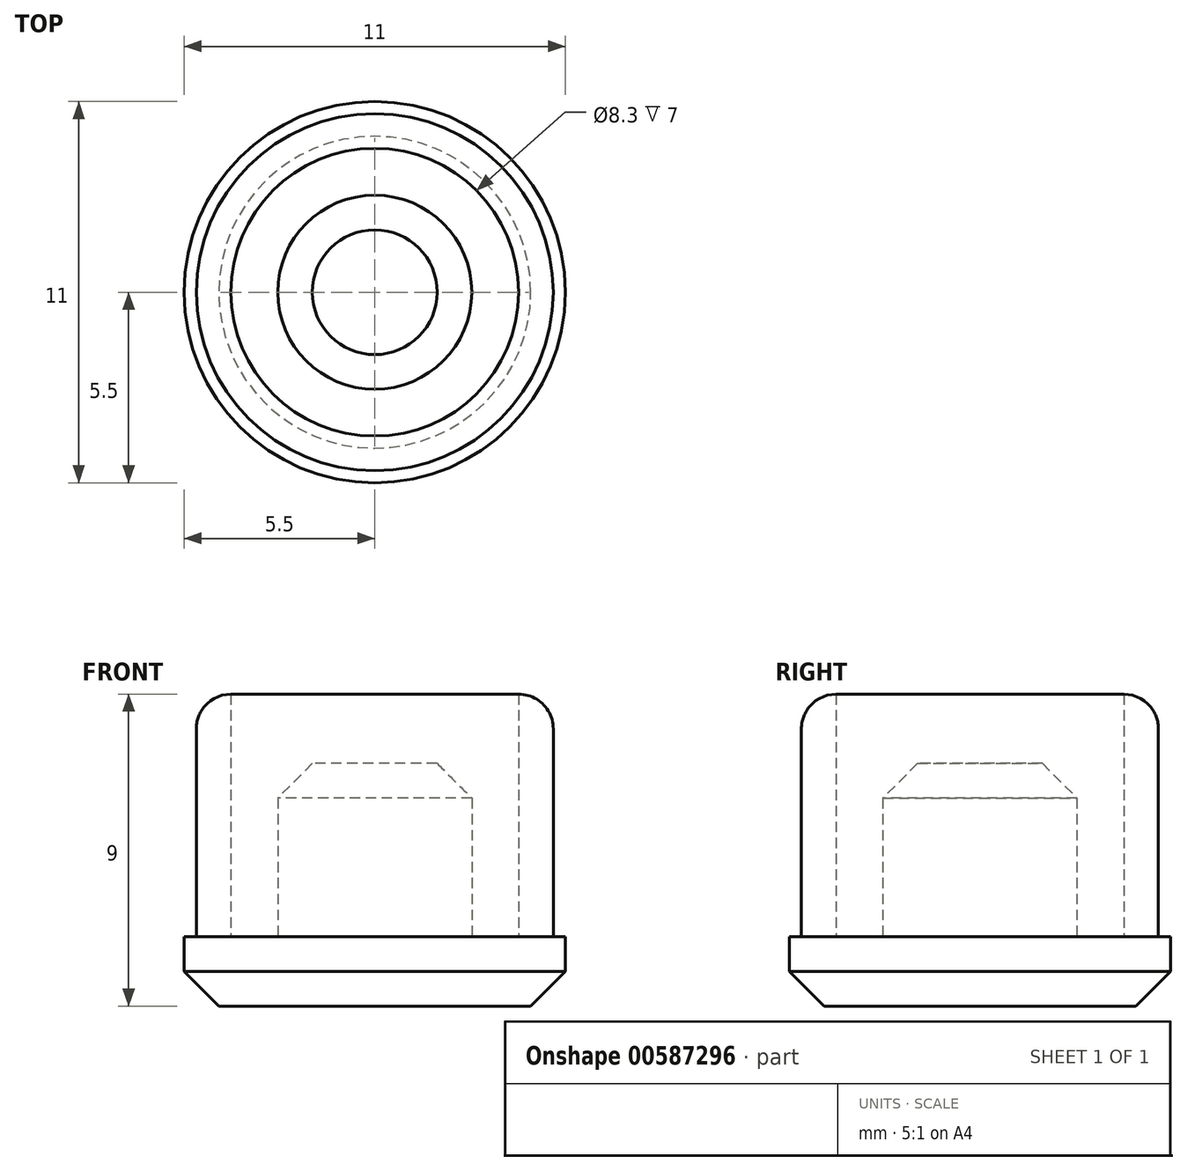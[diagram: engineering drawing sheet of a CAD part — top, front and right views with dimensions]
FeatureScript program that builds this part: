
annotation { "Feature Type Name" : "Feature", "Feature Type Description" : "" }
export const myFeature = defineFeature(function(context is Context, id is Id, definition is map)
    precondition{}
    {
        {
            var Q0;
            Q0=qCreatedBy(makeId("Top.planeOp"),FACE);
            var sketch = newSketch(context, id + "F0", { "sketchPlane" : qUnion([Q0])});
            skCircle(sketch, "E0", {"center": v(0, 0) * mm, "radius": 5.5 * mm});
            skSolve(sketch);
        }
        {
            var Q0;
            Q0 = qSketchRegion(id + "F0", true);
            extrude(context, id + "F1", {"entities" : qUnion([Q0]), "depth" : 2 * mm, "offsetDistance" : 25 * mm});
        }
        {
            var Q0;
            Q0=makeQuery(id+"F1.opExtrude","CAP_FACE",FACE,{"disambiguationData":[OSD([sQuery(id+"F0.wireOp",EDGE,"E0")])],"isStart":false});
            var sketch = newSketch(context, id + "F2", { "sketchPlane" : qUnion([Q0])});
            skCircle(sketch, "E1", {"center": v(0, 0) * mm, "radius": 4.15 * mm});
            skCircle(sketch, "E2", {"center": v(0, 0) * mm, "radius": 2.8 * mm});
            skCircle(sketch, "E3.0", {"center": v(0, 0) * mm, "radius": 5.15 * mm});
            skSolve(sketch);
        }
        {
            var Q0;
            Q0=makeQuery(id+"F2.imprint","IMPRINT",FACE,{"disambiguationData":[TD([[makeQuery(id+"F2.imprint","IMPRINT",EDGE,{"derivedFrom":sQuery(id+"F2.wireOp",EDGE,"E2")}),1.0]])]});
            extrude(context, id + "F3", {"entities" : qUnion([Q0]), "operationType" : NewBodyOperationType.ADD, "depth" : 5 * mm, "offsetDistance" : 25 * mm});
        }
        {
            var Q0;
            Q0=makeQuery(id+"F2.imprint","IMPRINT",FACE,{"disambiguationData":[TD([[makeQuery(id+"F2.imprint","IMPRINT",EDGE,{"derivedFrom":sQuery(id+"F2.wireOp",EDGE,"E1")}),-1.0]])]});
            extrude(context, id + "F4", {"entities" : qUnion([Q0]), "operationType" : NewBodyOperationType.ADD, "depth" : 7 * mm, "offsetDistance" : 25 * mm});
        }
        {
            var Q0;
            Q0=makeQuery(id+"F3.opExtrude","CAP_EDGE",EDGE,{"disambiguationData":[OSD([sQuery(id+"F2.wireOp",EDGE,"E2")])],"isStart":false});
            chamfer(context, id + "F5", {"entities" : qUnion([Q0]), "chamferType" : ChamferType.OFFSET_ANGLE, "width" : 1 * mm, "oppositeDirection" : false, "angle" : 45 * degree, "tangentPropagation" : true});
        }
        {
            var Q0;
            Q0=makeQuery(id+"F4.opExtrude","CAP_EDGE",EDGE,{"disambiguationData":[OSD([sQuery(id+"F2.wireOp",EDGE,"E3.0")])],"isStart":false});
            fillet(context, id + "F6", {"entities" : qUnion([Q0]), "radius" : 1 * mm, "tangentPropagation" : true, "allowEdgeOverflow" : false});
        }
        {
            var Q0;
            Q0=makeQuery(id+"F1.opExtrude","CAP_EDGE",EDGE,{"disambiguationData":[OSD([sQuery(id+"F0.wireOp",EDGE,"E0")])],"isStart":true});
            chamfer(context, id + "F7", {"entities" : qUnion([Q0]), "width" : 1 * mm, "tangentPropagation" : true});
        }
    });
